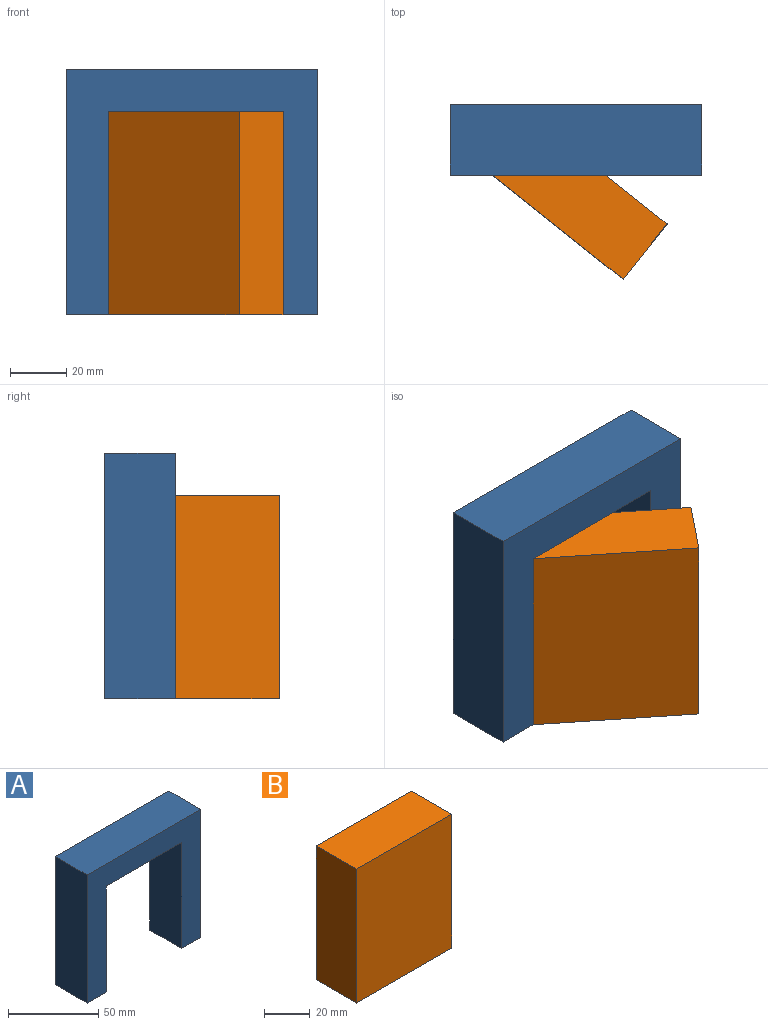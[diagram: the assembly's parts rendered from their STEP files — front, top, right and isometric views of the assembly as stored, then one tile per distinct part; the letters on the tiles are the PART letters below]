
ASSEMBLY  parts=2 mates=1
PART A: 10 faces, bbox 89.1x25x87 mm
  f0: plane 72.04x25mm, normal (-1,0,0), area 1801mm2, adj f1,f7,f8,f9
  f1: plane 25x15mm, normal (0,0,-1), area 375mm2, adj f0,f2,f8,f9
  f2: plane 87.04x25mm, normal (1,0,0), area 2176mm2, adj f1,f3,f8,f9
  f3: plane 89.11x25mm, normal (0,0,1), area 2227.8mm2, adj f2,f4,f8,f9
  f4: plane 87.04x25mm, normal (-1,0,0), area 2176mm2, adj f3,f5,f8,f9
  f5: plane 25x15mm, normal (0,0,-1), area 375mm2, adj f4,f6,f8,f9
  f6: plane 72.04x25mm, normal (1,0,0), area 1801mm2, adj f5,f7,f8,f9
  f7: plane 59.11x25mm, normal (0,0,-1), area 1477.8mm2, adj f0,f6,f8,f9
  f8: plane 89.11x87.04mm, normal (0,-1,0), area 3497.9mm2, adj f0,f1,f2,f3,f4,f5,f6,f7
  f9: plane 89.11x87.04mm, normal (0,1,0), area 3497.9mm2, adj f0,f1,f2,f3,f4,f5,f6,f7
PART B: 6 faces, bbox 59.1x25x72 mm
  f0: plane 72.04x25mm, normal (-1,0,0), area 1801mm2, adj f1,f3,f4,f5
  f1: plane 59.11x25mm, normal (0,0,-1), area 1477.8mm2, adj f0,f2,f4,f5
  f2: plane 72.04x25mm, normal (1,0,0), area 1801mm2, adj f1,f3,f4,f5
  f3: plane 59.11x25mm, normal (0,0,1), area 1477.8mm2, adj f0,f2,f4,f5
  f4: plane 72.04x59.11mm, normal (0,-1,0), area 4258.4mm2, adj f0,f1,f2,f3
  f5: plane 72.04x59.11mm, normal (0,1,0), area 4258.4mm2, adj f0,f1,f2,f3
PLACE A t=(-39.06,23.55,-31.7)mm fixed
PLACE B rot(axis=(0,0,-1),38.6deg) t=(-20.21,27.45,-31.7)mm
MATE revolute B.f3 <-> A.f7  axis (0,0,1) through (-24.06,-1.45,40.34)mm
